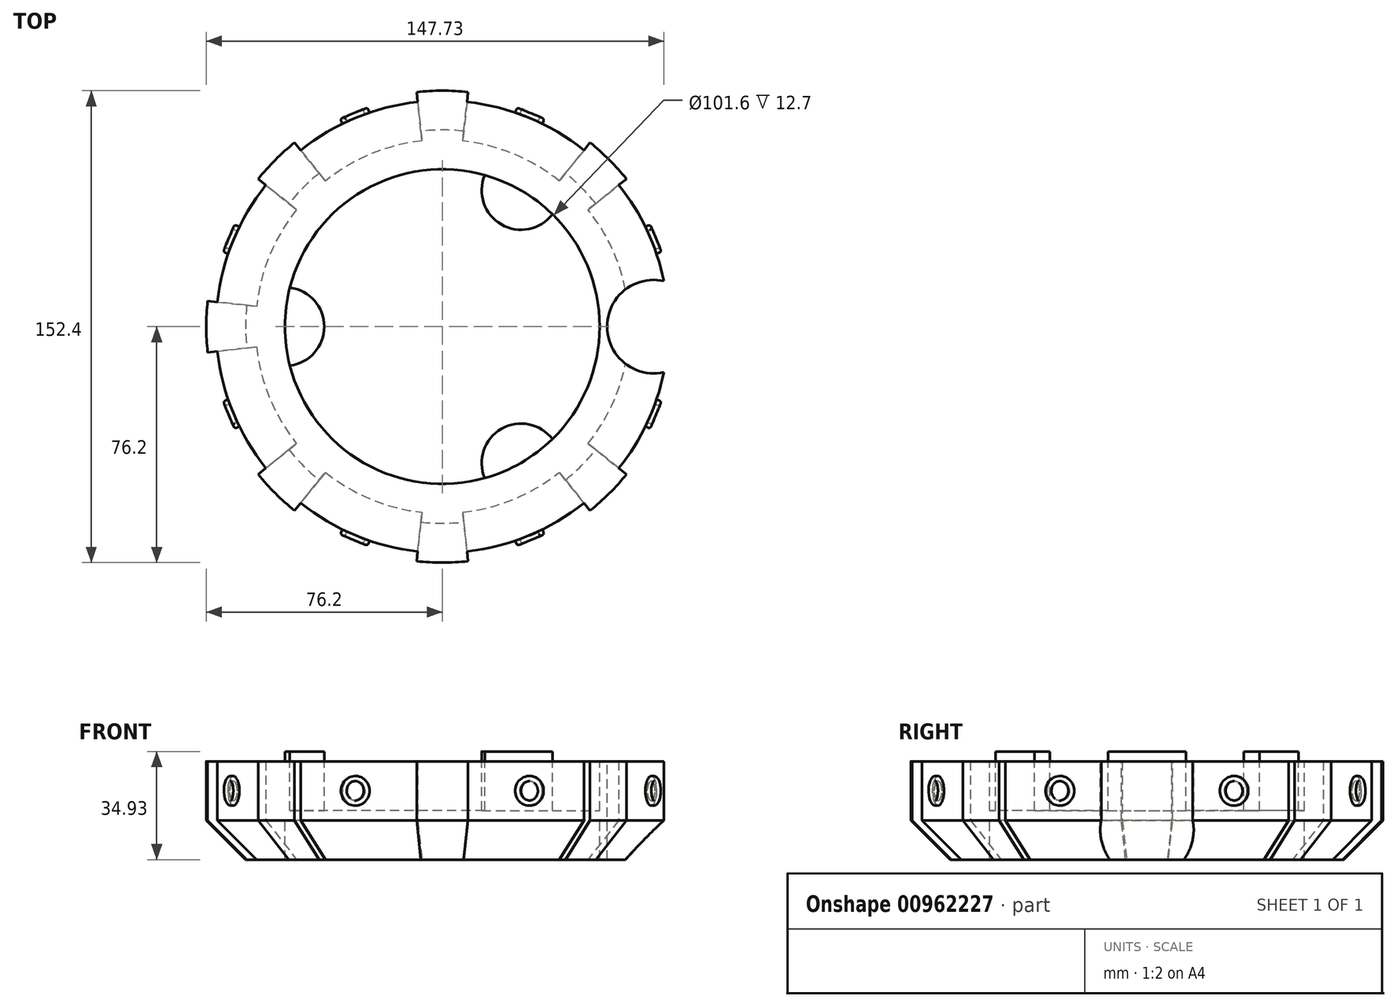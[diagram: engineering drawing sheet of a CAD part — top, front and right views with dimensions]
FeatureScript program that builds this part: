
annotation { "Feature Type Name" : "Feature", "Feature Type Description" : "" }
export const myFeature = defineFeature(function(context is Context, id is Id, definition is map)
    precondition{}
    {
        {
            var Q0;
            Q0=qCreatedBy(makeId("Front.planeOp"),FACE);
            var sketch = newSketch(context, id + "F0", { "sketchPlane" : qUnion([Q0])});
            skLineSegment(sketch, "E0", {"start": v(0, 78.32) * mm, "end": v(0, -69.21) * mm, "construction": true});
            skLineSegment(sketch, "E1", {"start": v(-73.03, 19.05) * mm, "end": v(-73.03, 0) * mm});
            skLineSegment(sketch, "E2", {"start": v(-73.03, 0) * mm, "end": v(-60.33, -12.7) * mm});
            skLineSegment(sketch, "E3", {"start": v(-60.33, -12.7) * mm, "end": v(-50.8, -12.7) * mm});
            skLineSegment(sketch, "E4", {"start": v(-50.8, -12.7) * mm, "end": v(-50.8, 19.05) * mm});
            skLineSegment(sketch, "E5", {"start": v(-50.8, 19.05) * mm, "end": v(-73.03, 19.05) * mm});
            skPoint(sketch, "E6", {"position": v(-50.8, 0) * mm});
            skSolve(sketch);
        }
        {
            var Q0;
            Q0=makeQuery(id+"F0.imprint","IMPRINT",FACE,{"disambiguationData":[TD([[makeQuery(id+"F0.imprint","IMPRINT",EDGE,{"derivedFrom":sQuery(id+"F0.wireOp",EDGE,"E1")}),1.0]])]});
            var Q1;
            Q1=sQuery(id+"F0.wireOp",EDGE,"E0");
            revolve(context, id + "F1", {"surfaceOperationType" : NewSurfaceOperationType.NEW, "entities" : qUnion([Q0]), "axis" : qUnion([Q1]), "revolveType" : RevolveType.FULL});
        }
        {
            var Q0;
            Q0=qCreatedBy(makeId("Front.planeOp"),FACE);
            var sketch = newSketch(context, id + "F2", { "sketchPlane" : qUnion([Q0])});
            skLineSegment(sketch, "E7.0", {"start": v(-73.03, 19.05) * mm, "end": v(-73.03, 0) * mm, "construction": true});
            skLineSegment(sketch, "E7.1", {"start": v(-73.03, 0) * mm, "end": v(-60.33, -12.7) * mm, "construction": true});
            skLineSegment(sketch, "E8", {"start": v(-73.03, 19.05) * mm, "end": v(-73.03, 0) * mm});
            skLineSegment(sketch, "E9", {"start": v(-60.33, -12.7) * mm, "end": v(-63.5, -12.7) * mm});
            skLineSegment(sketch, "E10", {"start": v(-63.5, -12.7) * mm, "end": v(-76.2, 0) * mm});
            skLineSegment(sketch, "E11", {"start": v(-76.2, 0) * mm, "end": v(-76.2, 19.05) * mm});
            skLineSegment(sketch, "E12", {"start": v(-76.2, 19.05) * mm, "end": v(-73.03, 19.05) * mm});
            skLineSegment(sketch, "E13.0", {"start": v(0, 78.32) * mm, "end": v(0, -69.21) * mm, "construction": true});
            skLineSegment(sketch, "E14", {"start": v(-73.03, 0) * mm, "end": v(-60.33, -12.7) * mm});
            skSolve(sketch);
        }
        {
            var Q0;
            Q0=makeQuery(id+"F2.imprint","IMPRINT",FACE,{"disambiguationData":[TD([[makeQuery(id+"F2.imprint","IMPRINT",EDGE,{"derivedFrom":sQuery(id+"F2.wireOp",EDGE,"E8")}),-1.0]])]});
            var Q1;
            Q1=sQuery(id+"F2.wireOp",EDGE,"E13.0");
            revolve(context, id + "F3", {"surfaceOperationType" : NewSurfaceOperationType.NEW, "entities" : qUnion([Q0]), "axis" : qUnion([Q1]), "revolveType" : RevolveType.SYMMETRIC, "angle" : 12.5 * degree});
        }
        {
            var Q0;
            Q0=qCreatedBy(makeId("Front.planeOp"),FACE);
            var Q1;
            Q1=sQuery(id+"F2.wireOp",EDGE,"E13.0");
            cPlane(context, id + "F4", {"entities" : qUnion([Q0, Q1]), "cplaneType" : CPlaneType.LINE_ANGLE, "offset" : 25.4 * mm, "angle" : 22.5 * degree, "oppositeDirection" : true, "width" : 152.4 * mm, "height" : 152.4 * mm});
        }
        {
            var Q0;
            Q0=qCreatedBy(id+"F4.planeOp",FACE);
            var Q1;
            Q1=sQuery(id+"F2.wireOp",EDGE,"E13.0");
            cPlane(context, id + "F5", {"entities" : qUnion([Q0, Q1]), "cplaneType" : CPlaneType.LINE_ANGLE, "offset" : 25.4 * mm, "angle" : 90 * degree, "width" : 152.4 * mm, "height" : 152.4 * mm});
        }
        {
            var Q0;
            Q0=qCreatedBy(id+"F5.planeOp",FACE);
            cPlane(context, id + "F6", {"entities" : qUnion([Q0]), "cplaneType" : CPlaneType.OFFSET, "offset" : 74.61 * mm, "width" : 152.4 * mm, "height" : 152.4 * mm});
        }
        {
            var Q0;
            Q0=qCreatedBy(id+"F6.planeOp",FACE);
            var sketch = newSketch(context, id + "F7", { "sketchPlane" : qUnion([Q0])});
            skCircle(sketch, "E15", {"center": v(0, 9.53) * mm, "radius": 3.18 * mm});
            skCircle(sketch, "E16", {"center": v(0, 9.53) * mm, "radius": 4.76 * mm});
            skSolve(sketch);
        }
        {
            var Q0;
            Q0=makeQuery(id+"F7.imprint","IMPRINT",FACE,{"disambiguationData":[TD([[makeQuery(id+"F7.imprint","IMPRINT",EDGE,{"derivedFrom":sQuery(id+"F7.wireOp",EDGE,"E15")}),-1.0]])]});
            extrude(context, id + "F8", {"entities" : qUnion([Q0]), "oppositeDirection" : true, "depth" : 3.17 * mm, "offsetDistance" : 25.4 * mm});
        }
        {
            var Q0;
            Q0=makeQuery(id+"F8.opExtrude","CAP_EDGE",EDGE,{"disambiguationData":[OSD([sQuery(id+"F7.wireOp",EDGE,"E16")])],"isStart":true});
            var Q1;
            Q1=makeQuery(id+"F8.opExtrude","CAP_EDGE",EDGE,{"disambiguationData":[OSD([sQuery(id+"F7.wireOp",EDGE,"E15")])],"isStart":true});
            fillet(context, id + "F9", {"entities" : qUnion([Q0, Q1]), "radius" : 0.8 * mm, "tangentPropagation" : true, "allowEdgeOverflow" : false});
        }
        {
            var Q0;
            Q0=makeQuery(id+"F3.opRevolve","SWEPT_BODY",BODY,{"disambiguationData":[OSD([sQuery(id+"F2.wireOp",EDGE,"E8"),sQuery(id+"F2.wireOp",EDGE,"E9"),sQuery(id+"F2.wireOp",EDGE,"E10"),sQuery(id+"F2.wireOp",EDGE,"E11"),sQuery(id+"F2.wireOp",EDGE,"E12"),sQuery(id+"F2.wireOp",EDGE,"E14")])]});
            var Q1;
            Q1=makeQuery(id+"F8.opExtrude","SWEPT_BODY",BODY,{"disambiguationData":[OSD([sQuery(id+"F7.wireOp",EDGE,"E15"),sQuery(id+"F7.wireOp",EDGE,"E16")])]});
            var Q2;
            Q2=sQuery(id+"F0.wireOp",EDGE,"E0");
            circularPattern(context, id + "F10", {"entities" : qUnion([Q0, Q1]), "axis" : qUnion([Q2]), "angle" : 360 * degree, "instanceCount" : 8, "equalSpace" : true});
        }
        {
            var Q0;
            Q0=qCreatedBy(makeId("Top.planeOp"),FACE);
            var sketch = newSketch(context, id + "F11", { "sketchPlane" : qUnion([Q0])});
            skCircle(sketch, "E17", {"center": v(0, 0) * mm, "radius": 50.8 * mm});
            skSolve(sketch);
        }
        {
            var Q0;
            Q0 = qSketchRegion(id + "F11", true);
            extrude(context, id + "F12", {"entities" : qUnion([Q0]), "operationType" : NewBodyOperationType.ADD, "depth" : 3.17 * mm, "offsetDistance" : 25.4 * mm});
        }
        {
            var Q0;
            Q0=makeQuery(id+"F1.opRevolve","SWEPT_FACE",FACE,{"disambiguationData":[OSD([sQuery(id+"F0.wireOp",EDGE,"E5")])]});
            var sketch = newSketch(context, id + "F13", { "sketchPlane" : qUnion([Q0])});
            skArc(sketch, "E18", {"start": v(-49.21, 12.6) * mm, "mid": v(-50.8, 0) * mm, "end": v(-49.21, -12.6) * mm});
            skArc(sketch, "E19", {"start": v(-49.21, -12.6) * mm, "mid": v(-38.1, 0) * mm, "end": v(-49.21, 12.6) * mm});
            skArc(sketch, "E20.1.0", {"start": v(35.52, -36.32) * mm, "mid": v(19.05, -33) * mm, "end": v(13.7, -48.92) * mm});
            skArc(sketch, "E20.2.0", {"start": v(13.7, 48.92) * mm, "mid": v(19.05, 33) * mm, "end": v(35.52, 36.32) * mm});
            skArc(sketch, "E21.trimOffspring", {"start": v(35.52, 36.32) * mm, "mid": v(25.4, 44) * mm, "end": v(13.7, 48.92) * mm});
            skArc(sketch, "E22.trimOffspring", {"start": v(13.7, -48.92) * mm, "mid": v(25.4, -44) * mm, "end": v(35.52, -36.32) * mm});
            skSolve(sketch);
        }
        {
            var Q0;
            Q0=makeQuery(id+"F13.imprint","IMPRINT",FACE,{"disambiguationData":[TD([[makeQuery(id+"F13.imprint","IMPRINT",EDGE,{"derivedFrom":sQuery(id+"F13.wireOp",EDGE,"E18")}),1.0]])]});
            var Q1;
            Q1=makeQuery(id+"F13.imprint","IMPRINT",FACE,{"disambiguationData":[TD([[makeQuery(id+"F13.imprint","IMPRINT",EDGE,{"derivedFrom":sQuery(id+"F13.wireOp",EDGE,"E20.2.0")}),1.0]])]});
            var Q2;
            Q2=makeQuery(id+"F13.imprint","IMPRINT",FACE,{"disambiguationData":[TD([[makeQuery(id+"F13.imprint","IMPRINT",EDGE,{"derivedFrom":sQuery(id+"F13.wireOp",EDGE,"E20.1.0")}),1.0]])]});
            extrude(context, id + "F14", {"entities" : qUnion([Q0, Q1, Q2]), "operationType" : NewBodyOperationType.ADD, "oppositeDirection" : true, "depth" : 15.88 * mm, "offsetDistance" : 25.4 * mm, "hasSecondDirection" : true, "secondDirectionOppositeDirection" : false, "secondDirectionDepth" : 3.17 * mm});
        }
        {
            var Q0;
            Q0=makeQuery(id+"F1.opRevolve","SWEPT_BODY",BODY,{"disambiguationData":[OSD([sQuery(id+"F0.wireOp",EDGE,"E1"),sQuery(id+"F0.wireOp",EDGE,"E2"),sQuery(id+"F0.wireOp",EDGE,"E3"),sQuery(id+"F0.wireOp",EDGE,"E4"),sQuery(id+"F0.wireOp",EDGE,"E5")])]});
            var Q1;
            Q1=makeQuery(id+"F3.opRevolve","SWEPT_BODY",BODY,{"disambiguationData":[OSD([sQuery(id+"F2.wireOp",EDGE,"E8"),sQuery(id+"F2.wireOp",EDGE,"E9"),sQuery(id+"F2.wireOp",EDGE,"E10"),sQuery(id+"F2.wireOp",EDGE,"E11"),sQuery(id+"F2.wireOp",EDGE,"E12"),sQuery(id+"F2.wireOp",EDGE,"E14")])]});
            var Q2;
            Q2=makeQuery(id+"F8.opExtrude","SWEPT_BODY",BODY,{"disambiguationData":[OSD([sQuery(id+"F7.wireOp",EDGE,"E15"),sQuery(id+"F7.wireOp",EDGE,"E16")])]});
            var Q3;
            Q3=makeQuery(id+"F10.opPattern","COPY",BODY,{"derivedFrom":makeQuery(id+"F3.opRevolve","SWEPT_BODY",BODY,{"disambiguationData":[OSD([sQuery(id+"F2.wireOp",EDGE,"E8"),sQuery(id+"F2.wireOp",EDGE,"E9"),sQuery(id+"F2.wireOp",EDGE,"E10"),sQuery(id+"F2.wireOp",EDGE,"E11"),sQuery(id+"F2.wireOp",EDGE,"E12"),sQuery(id+"F2.wireOp",EDGE,"E14")])]}),"instanceName":"1"});
            var Q4;
            Q4=makeQuery(id+"F10.opPattern","COPY",BODY,{"derivedFrom":makeQuery(id+"F8.opExtrude","SWEPT_BODY",BODY,{"disambiguationData":[OSD([sQuery(id+"F7.wireOp",EDGE,"E15"),sQuery(id+"F7.wireOp",EDGE,"E16")])]}),"instanceName":"1"});
            var Q5;
            Q5=makeQuery(id+"F10.opPattern","COPY",BODY,{"derivedFrom":makeQuery(id+"F3.opRevolve","SWEPT_BODY",BODY,{"disambiguationData":[OSD([sQuery(id+"F2.wireOp",EDGE,"E8"),sQuery(id+"F2.wireOp",EDGE,"E9"),sQuery(id+"F2.wireOp",EDGE,"E10"),sQuery(id+"F2.wireOp",EDGE,"E11"),sQuery(id+"F2.wireOp",EDGE,"E12"),sQuery(id+"F2.wireOp",EDGE,"E14")])]}),"instanceName":"2"});
            var Q6;
            Q6=makeQuery(id+"F10.opPattern","COPY",BODY,{"derivedFrom":makeQuery(id+"F8.opExtrude","SWEPT_BODY",BODY,{"disambiguationData":[OSD([sQuery(id+"F7.wireOp",EDGE,"E15"),sQuery(id+"F7.wireOp",EDGE,"E16")])]}),"instanceName":"2"});
            var Q7;
            Q7=makeQuery(id+"F10.opPattern","COPY",BODY,{"derivedFrom":makeQuery(id+"F3.opRevolve","SWEPT_BODY",BODY,{"disambiguationData":[OSD([sQuery(id+"F2.wireOp",EDGE,"E8"),sQuery(id+"F2.wireOp",EDGE,"E9"),sQuery(id+"F2.wireOp",EDGE,"E10"),sQuery(id+"F2.wireOp",EDGE,"E11"),sQuery(id+"F2.wireOp",EDGE,"E12"),sQuery(id+"F2.wireOp",EDGE,"E14")])]}),"instanceName":"3"});
            var Q8;
            Q8=makeQuery(id+"F10.opPattern","COPY",BODY,{"derivedFrom":makeQuery(id+"F8.opExtrude","SWEPT_BODY",BODY,{"disambiguationData":[OSD([sQuery(id+"F7.wireOp",EDGE,"E15"),sQuery(id+"F7.wireOp",EDGE,"E16")])]}),"instanceName":"3"});
            var Q9;
            Q9=makeQuery(id+"F10.opPattern","COPY",BODY,{"derivedFrom":makeQuery(id+"F3.opRevolve","SWEPT_BODY",BODY,{"disambiguationData":[OSD([sQuery(id+"F2.wireOp",EDGE,"E8"),sQuery(id+"F2.wireOp",EDGE,"E9"),sQuery(id+"F2.wireOp",EDGE,"E10"),sQuery(id+"F2.wireOp",EDGE,"E11"),sQuery(id+"F2.wireOp",EDGE,"E12"),sQuery(id+"F2.wireOp",EDGE,"E14")])]}),"instanceName":"4"});
            var Q10;
            Q10=makeQuery(id+"F10.opPattern","COPY",BODY,{"derivedFrom":makeQuery(id+"F8.opExtrude","SWEPT_BODY",BODY,{"disambiguationData":[OSD([sQuery(id+"F7.wireOp",EDGE,"E15"),sQuery(id+"F7.wireOp",EDGE,"E16")])]}),"instanceName":"4"});
            var Q11;
            Q11=makeQuery(id+"F10.opPattern","COPY",BODY,{"derivedFrom":makeQuery(id+"F3.opRevolve","SWEPT_BODY",BODY,{"disambiguationData":[OSD([sQuery(id+"F2.wireOp",EDGE,"E8"),sQuery(id+"F2.wireOp",EDGE,"E9"),sQuery(id+"F2.wireOp",EDGE,"E10"),sQuery(id+"F2.wireOp",EDGE,"E11"),sQuery(id+"F2.wireOp",EDGE,"E12"),sQuery(id+"F2.wireOp",EDGE,"E14")])]}),"instanceName":"5"});
            var Q12;
            Q12=makeQuery(id+"F10.opPattern","COPY",BODY,{"derivedFrom":makeQuery(id+"F8.opExtrude","SWEPT_BODY",BODY,{"disambiguationData":[OSD([sQuery(id+"F7.wireOp",EDGE,"E15"),sQuery(id+"F7.wireOp",EDGE,"E16")])]}),"instanceName":"5"});
            var Q13;
            Q13=makeQuery(id+"F10.opPattern","COPY",BODY,{"derivedFrom":makeQuery(id+"F3.opRevolve","SWEPT_BODY",BODY,{"disambiguationData":[OSD([sQuery(id+"F2.wireOp",EDGE,"E8"),sQuery(id+"F2.wireOp",EDGE,"E9"),sQuery(id+"F2.wireOp",EDGE,"E10"),sQuery(id+"F2.wireOp",EDGE,"E11"),sQuery(id+"F2.wireOp",EDGE,"E12"),sQuery(id+"F2.wireOp",EDGE,"E14")])]}),"instanceName":"6"});
            var Q14;
            Q14=makeQuery(id+"F10.opPattern","COPY",BODY,{"derivedFrom":makeQuery(id+"F8.opExtrude","SWEPT_BODY",BODY,{"disambiguationData":[OSD([sQuery(id+"F7.wireOp",EDGE,"E15"),sQuery(id+"F7.wireOp",EDGE,"E16")])]}),"instanceName":"6"});
            var Q15;
            Q15=makeQuery(id+"F10.opPattern","COPY",BODY,{"derivedFrom":makeQuery(id+"F3.opRevolve","SWEPT_BODY",BODY,{"disambiguationData":[OSD([sQuery(id+"F2.wireOp",EDGE,"E8"),sQuery(id+"F2.wireOp",EDGE,"E9"),sQuery(id+"F2.wireOp",EDGE,"E10"),sQuery(id+"F2.wireOp",EDGE,"E11"),sQuery(id+"F2.wireOp",EDGE,"E12"),sQuery(id+"F2.wireOp",EDGE,"E14")])]}),"instanceName":"7"});
            var Q16;
            Q16=makeQuery(id+"F10.opPattern","COPY",BODY,{"derivedFrom":makeQuery(id+"F8.opExtrude","SWEPT_BODY",BODY,{"disambiguationData":[OSD([sQuery(id+"F7.wireOp",EDGE,"E15"),sQuery(id+"F7.wireOp",EDGE,"E16")])]}),"instanceName":"7"});
            booleanBodies(context, id + "F15", {"operationType" : BooleanOperationType.UNION, "tools" : qUnion([Q0, Q1, Q2, Q3, Q4, Q5, Q6, Q7, Q8, Q9, Q10, Q11, Q12, Q13, Q14, Q15, Q16])});
        }
        {
            var Q0;
            {var subQ0=makeQuery(id+"F3.opRevolve","SWEPT_FACE",FACE,{"disambiguationData":[OSD([sQuery(id+"F2.wireOp",EDGE,"E12")])]});Q0=makeQuery(id+"F15.opBoolean","MERGE",FACE,{"derivedFrom":[makeQuery(id+"F1.opRevolve","SWEPT_FACE",FACE,{"disambiguationData":[OSD([sQuery(id+"F0.wireOp",EDGE,"E5")])]}),subQ0,makeQuery(id+"F10.opPattern","COPY",FACE,{"derivedFrom":subQ0,"instanceName":"1"}),makeQuery(id+"F10.opPattern","COPY",FACE,{"derivedFrom":subQ0,"instanceName":"2"}),makeQuery(id+"F10.opPattern","COPY",FACE,{"derivedFrom":subQ0,"instanceName":"3"}),makeQuery(id+"F10.opPattern","COPY",FACE,{"derivedFrom":subQ0,"instanceName":"4"}),makeQuery(id+"F10.opPattern","COPY",FACE,{"derivedFrom":subQ0,"instanceName":"5"}),makeQuery(id+"F10.opPattern","COPY",FACE,{"derivedFrom":subQ0,"instanceName":"6"}),makeQuery(id+"F10.opPattern","COPY",FACE,{"derivedFrom":subQ0,"instanceName":"7"})]});}
            var sketch = newSketch(context, id + "F16", { "sketchPlane" : qUnion([Q0])});
            skCircle(sketch, "E23", {"center": v(68.26, 0) * mm, "radius": 15.08 * mm});
            skSolve(sketch);
        }
        {
            var Q0;
            Q0 = qSketchRegion(id + "F16", true);
            extrude(context, id + "F17", {"entities" : qUnion([Q0]), "operationType" : NewBodyOperationType.REMOVE, "oppositeDirection" : true, "depth" : 31.75 * mm, "offsetDistance" : 25.4 * mm});
        }
    });
